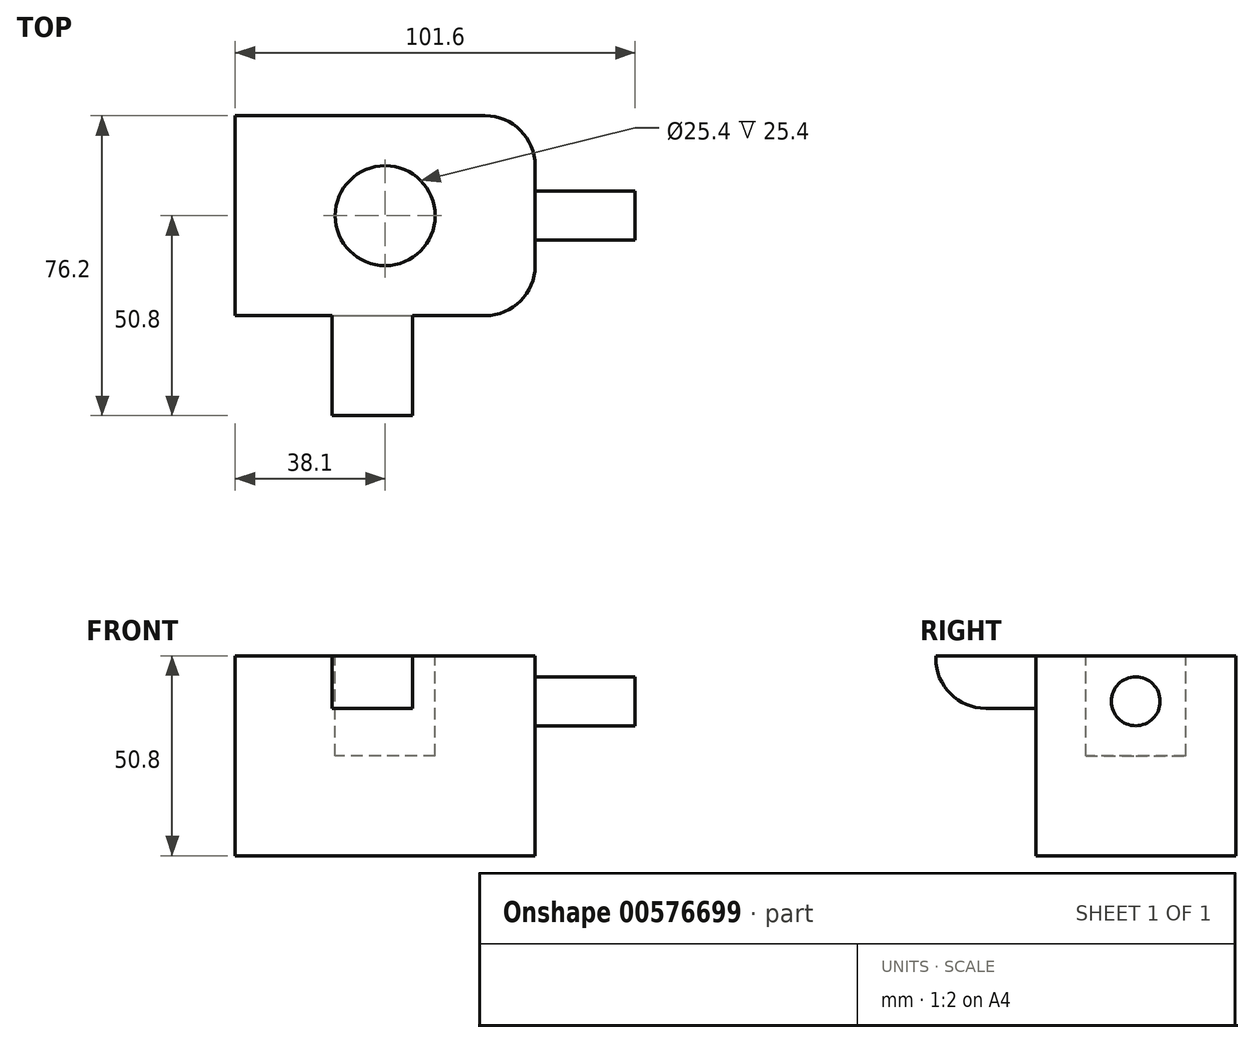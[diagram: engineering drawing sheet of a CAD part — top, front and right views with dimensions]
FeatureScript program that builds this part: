
annotation { "Feature Type Name" : "Feature", "Feature Type Description" : "" }
export const myFeature = defineFeature(function(context is Context, id is Id, definition is map)
    precondition{}
    {
        {
            var Q0;
            Q0=qCreatedBy(makeId("Top.planeOp"),FACE);
            var sketch = newSketch(context, id + "F0", { "sketchPlane" : qUnion([Q0])});
            skLineSegment(sketch, "E0.bottom", {"start": v(-38.1, 25.4) * mm, "end": v(38.1, 25.4) * mm});
            skLineSegment(sketch, "E0.top", {"start": v(-38.1, -25.4) * mm, "end": v(38.1, -25.4) * mm});
            skLineSegment(sketch, "E0.left", {"start": v(-38.1, 25.4) * mm, "end": v(-38.1, -25.4) * mm});
            skLineSegment(sketch, "E0.right", {"start": v(38.1, 25.4) * mm, "end": v(38.1, -25.4) * mm});
            skSolve(sketch);
        }
        {
            var Q0;
            Q0=makeQuery(id+"F0.imprint","IMPRINT",FACE,{"disambiguationData":[TD([[makeQuery(id+"F0.imprint","IMPRINT",EDGE,{"derivedFrom":sQuery(id+"F0.wireOp",EDGE,"E0.bottom")}),-1.0]])]});
            extrude(context, id + "F1", {"entities" : qUnion([Q0]), "depth" : 50.8 * mm, "offsetDistance" : 25.4 * mm});
        }
        {
            var Q0;
            Q0=makeQuery(id+"F1.opExtrude","CAP_FACE",FACE,{"disambiguationData":[OSD([sQuery(id+"F0.wireOp",EDGE,"E0.bottom"),sQuery(id+"F0.wireOp",EDGE,"E0.top"),sQuery(id+"F0.wireOp",EDGE,"E0.left"),sQuery(id+"F0.wireOp",EDGE,"E0.right")])],"isStart":false});
            var sketch = newSketch(context, id + "F2", { "sketchPlane" : qUnion([Q0])});
            skCircle(sketch, "E1", {"center": v(0, 0) * mm, "radius": 12.7 * mm});
            skSolve(sketch);
        }
        {
            var Q0;
            Q0=makeQuery(id+"F2.imprint","IMPRINT",FACE,{"disambiguationData":[TD([[makeQuery(id+"F2.imprint","IMPRINT",EDGE,{"derivedFrom":sQuery(id+"F2.wireOp",EDGE,"E1")}),1.0]])]});
            extrude(context, id + "F3", {"entities" : qUnion([Q0]), "operationType" : NewBodyOperationType.REMOVE, "oppositeDirection" : true, "depth" : 25.4 * mm, "offsetDistance" : 25.4 * mm});
        }
        {
            var Q0;
            Q0=makeQuery(id+"F1.opExtrude","SWEPT_EDGE",EDGE,{"disambiguationData":[OSD([sQuery(id+"F0.wireOp",EDGE,"E0.top"),sQuery(id+"F0.wireOp",EDGE,"E0.right")])]});
            var Q1;
            Q1=makeQuery(id+"F1.opExtrude","SWEPT_EDGE",EDGE,{"disambiguationData":[OSD([sQuery(id+"F0.wireOp",EDGE,"E0.bottom"),sQuery(id+"F0.wireOp",EDGE,"E0.right")])]});
            fillet(context, id + "F4", {"entities" : qUnion([Q0, Q1]), "radius" : 12.7 * mm, "tangentPropagation" : true, "allowEdgeOverflow" : false});
        }
        {
            var Q0;
            Q0=makeQuery(id+"F1.opExtrude","SWEPT_FACE",FACE,{"disambiguationData":[OSD([sQuery(id+"F0.wireOp",EDGE,"E0.top")])]});
            var sketch = newSketch(context, id + "F5", { "sketchPlane" : qUnion([Q0])});
            skLineSegment(sketch, "E2.bottom", {"start": v(-13.5, 50.8) * mm, "end": v(6.98, 50.8) * mm});
            skLineSegment(sketch, "E2.top", {"start": v(-13.5, 37.46) * mm, "end": v(6.98, 37.46) * mm});
            skLineSegment(sketch, "E2.left", {"start": v(-13.5, 50.8) * mm, "end": v(-13.5, 37.46) * mm});
            skLineSegment(sketch, "E2.right", {"start": v(6.98, 50.8) * mm, "end": v(6.98, 37.46) * mm});
            skSolve(sketch);
        }
        {
            var Q0;
            Q0=makeQuery(id+"F5.imprint","IMPRINT",FACE,{"disambiguationData":[TD([[makeQuery(id+"F5.imprint","IMPRINT",EDGE,{"derivedFrom":sQuery(id+"F5.wireOp",EDGE,"E2.bottom")}),-1.0]])]});
            extrude(context, id + "F6", {"entities" : qUnion([Q0]), "operationType" : NewBodyOperationType.ADD, "depth" : 25.4 * mm, "offsetDistance" : 25.4 * mm});
        }
        {
            var Q0;
            Q0=makeQuery(id+"F6.opExtrude","CAP_EDGE",EDGE,{"disambiguationData":[OSD([sQuery(id+"F5.wireOp",EDGE,"E2.top")])],"isStart":false});
            fillet(context, id + "F7", {"entities" : qUnion([Q0]), "radius" : 12.7 * mm, "tangentPropagation" : true, "allowEdgeOverflow" : false});
        }
        {
            var Q0;
            Q0=makeQuery(id+"F1.opExtrude","SWEPT_FACE",FACE,{"disambiguationData":[OSD([sQuery(id+"F0.wireOp",EDGE,"E0.right")])]});
            var sketch = newSketch(context, id + "F8", { "sketchPlane" : qUnion([Q0])});
            skCircle(sketch, "E3", {"center": v(0, 39.24) * mm, "radius": 6.21 * mm});
            skSolve(sketch);
        }
        {
            var Q0;
            Q0=makeQuery(id+"F8.imprint","IMPRINT",FACE,{"disambiguationData":[TD([[makeQuery(id+"F8.imprint","IMPRINT",EDGE,{"derivedFrom":sQuery(id+"F8.wireOp",EDGE,"E3")}),1.0]])]});
            extrude(context, id + "F9", {"entities" : qUnion([Q0]), "operationType" : NewBodyOperationType.ADD, "depth" : 25.4 * mm, "offsetDistance" : 25.4 * mm});
        }
    });
